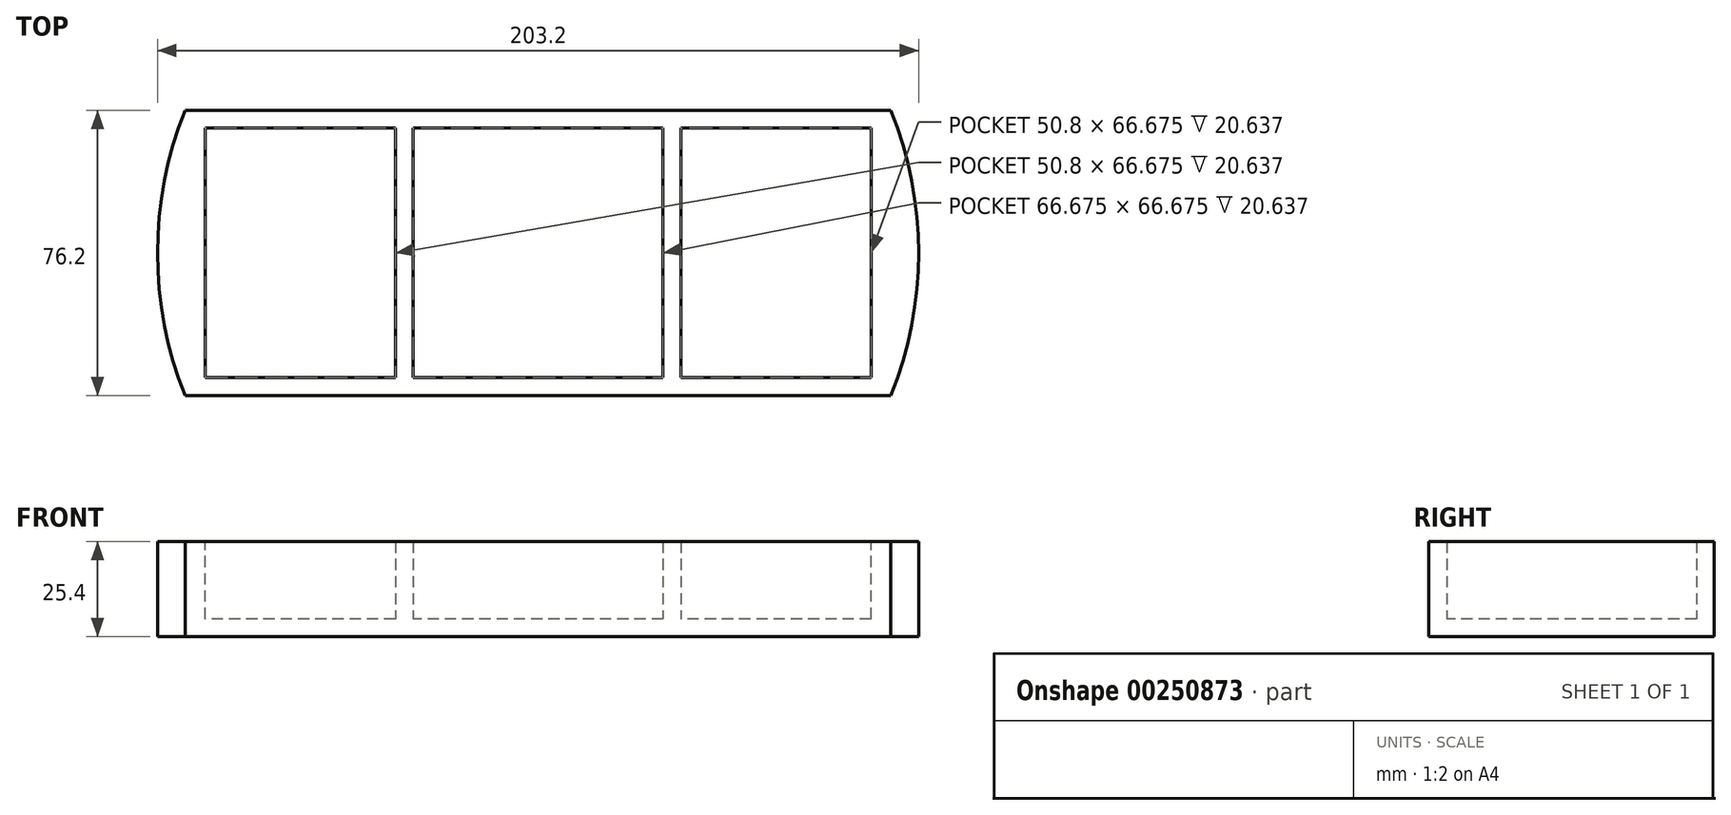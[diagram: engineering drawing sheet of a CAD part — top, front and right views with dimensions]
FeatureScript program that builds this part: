
annotation { "Feature Type Name" : "Feature", "Feature Type Description" : "" }
export const myFeature = defineFeature(function(context is Context, id is Id, definition is map)
    precondition{}
    {
        {
            var Q0;
            Q0=qCreatedBy(makeId("Top.planeOp"),FACE);
            var sketch = newSketch(context, id + "F0", { "sketchPlane" : qUnion([Q0])});
            skLineSegment(sketch, "E0.bottom", {"start": v(7.41, 0) * mm, "end": v(195.79, 0) * mm});
            skLineSegment(sketch, "E0.top", {"start": v(7.41, -76.2) * mm, "end": v(195.79, -76.2) * mm});
            skArc(sketch, "E1", {"start": v(7.41, 0) * mm, "mid": v(0, -38.1) * mm, "end": v(7.41, -76.2) * mm});
            skPoint(sketch, "E1.centerSnap0", {"position": v(101.6, 0) * mm});
            skPoint(sketch, "E1.centerSnap1", {"position": v(0, -38.1) * mm});
            skArc(sketch, "E2.trimOffspring", {"start": v(195.79, -76.2) * mm, "mid": v(203.2, -38.1) * mm, "end": v(195.79, 0) * mm});
            skPoint(sketch, "E0.left.start.orphan", {"position": v(0, 0) * mm});
            skSolve(sketch);
        }
        {
            var Q0;
            Q0=qSketchRegion(id+"F0",true);
            extrude(context, id + "F1", {"entities" : qUnion([Q0]), "depth" : 25.4 * mm});
        }
        {
            var Q0;
            Q0=makeQuery(id+"F1.opExtrude","CAP_FACE",FACE,{"disambiguationData":[OSD([sQuery(id+"F0.wireOp",EDGE,"E0.bottom"),sQuery(id+"F0.wireOp",EDGE,"E0.top"),sQuery(id+"F0.wireOp",EDGE,"E1"),sQuery(id+"F0.wireOp",EDGE,"E2.trimOffspring")])],"isStart":false});
            var sketch = newSketch(context, id + "F2", { "sketchPlane" : qUnion([Q0])});
            skLineSegment(sketch, "E3", {"start": v(12.7, 0) * mm, "end": v(12.7, -76.2) * mm});
            skLineSegment(sketch, "E4", {"start": v(15.88, -38.1) * mm, "end": v(15.88, -71.44) * mm});
            skLineSegment(sketch, "E5", {"start": v(15.88, -38.1) * mm, "end": v(15.88, -4.76) * mm});
            skLineSegment(sketch, "E6", {"start": v(15.88, -71.44) * mm, "end": v(12.7, -71.44) * mm});
            skLineSegment(sketch, "E7", {"start": v(15.88, -4.76) * mm, "end": v(12.7, -4.76) * mm});
            skLineSegment(sketch, "E8.MirrorCS", {"start": v(190.5, 0) * mm, "end": v(190.5, -76.2) * mm});
            skLineSegment(sketch, "E9.MirrorCS", {"start": v(187.33, -38.1) * mm, "end": v(187.33, -4.76) * mm});
            skLineSegment(sketch, "E10.MirrorCS", {"start": v(187.33, -4.76) * mm, "end": v(190.5, -4.76) * mm});
            skLineSegment(sketch, "E11.MirrorCS", {"start": v(187.33, -71.44) * mm, "end": v(190.5, -71.44) * mm});
            skLineSegment(sketch, "E12.MirrorCS", {"start": v(187.33, -38.1) * mm, "end": v(187.33, -71.44) * mm});
            skLineSegment(sketch, "E13", {"start": v(15.88, -4.76) * mm, "end": v(187.33, -4.76) * mm});
            skLineSegment(sketch, "E14", {"start": v(187.33, -71.44) * mm, "end": v(15.88, -71.44) * mm});
            skSolve(sketch);
        }
        {
            var Q0;
            Q0=qSketchRegion(id+"F2",true);
            extrude(context, id + "F3", {"entities" : qUnion([Q0]), "operationType" : NewBodyOperationType.REMOVE, "oppositeDirection" : true, "depth" : 20.64 * mm});
        }
        {
            var Q0;
            Q0=makeQuery(id+"F3.boolean.opBoolean","COPY",FACE,{"derivedFrom":makeQuery(id+"F3.opExtrude","CAP_FACE",FACE,{"disambiguationData":[OSD([sQuery(id+"F2.wireOp",EDGE,"E3"),sQuery(id+"F2.wireOp",EDGE,"E6"),sQuery(id+"F2.wireOp",EDGE,"E7"),sQuery(id+"F2.wireOp",EDGE,"E8.MirrorCS"),sQuery(id+"F2.wireOp",EDGE,"E10.MirrorCS"),sQuery(id+"F2.wireOp",EDGE,"E11.MirrorCS"),sQuery(id+"F2.wireOp",EDGE,"E13"),sQuery(id+"F2.wireOp",EDGE,"E14")])],"isStart":false})});
            var sketch = newSketch(context, id + "F4", { "sketchPlane" : qUnion([Q0])});
            skLineSegment(sketch, "E15", {"start": v(63.5, -71.44) * mm, "end": v(63.5, -4.76) * mm});
            skLineSegment(sketch, "E16", {"start": v(68.26, -71.44) * mm, "end": v(68.26, -4.76) * mm});
            skLineSegment(sketch, "E17.MirrorCS", {"start": v(63.5, -4.76) * mm, "end": v(63.5, -71.44) * mm});
            skLineSegment(sketch, "E18.MirrorCS", {"start": v(68.26, -4.76) * mm, "end": v(68.26, -71.44) * mm});
            skLineSegment(sketch, "E19.MirrorCS", {"start": v(134.94, -4.76) * mm, "end": v(134.94, -71.44) * mm});
            skLineSegment(sketch, "E20.MirrorCS", {"start": v(139.7, -4.76) * mm, "end": v(139.7, -71.44) * mm});
            skLineSegment(sketch, "E21", {"start": v(63.5, -4.76) * mm, "end": v(68.26, -4.76) * mm});
            skLineSegment(sketch, "E22", {"start": v(134.94, -4.76) * mm, "end": v(139.7, -4.76) * mm});
            skLineSegment(sketch, "E23", {"start": v(139.7, -71.44) * mm, "end": v(134.94, -71.44) * mm});
            skLineSegment(sketch, "E24", {"start": v(68.26, -71.44) * mm, "end": v(63.5, -71.44) * mm});
            skSolve(sketch);
        }
        {
            var Q0;
            Q0=qSketchRegion(id+"F4",true);
            extrude(context, id + "F5", {"entities" : qUnion([Q0]), "operationType" : NewBodyOperationType.ADD, "depth" : 20.64 * mm});
        }
    });
